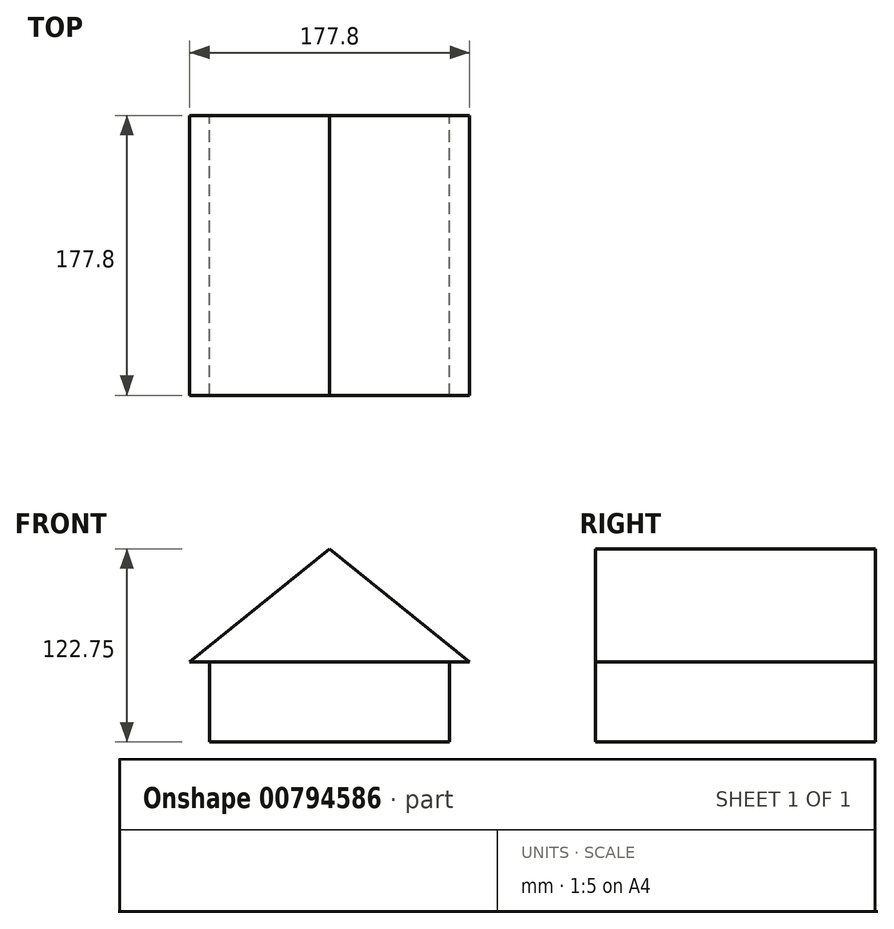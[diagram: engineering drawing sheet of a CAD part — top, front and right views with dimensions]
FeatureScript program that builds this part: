
annotation { "Feature Type Name" : "Feature", "Feature Type Description" : "" }
export const myFeature = defineFeature(function(context is Context, id is Id, definition is map)
    precondition{}
    {
        {
            var Q0;
            Q0=qCreatedBy(makeId("Front.planeOp"),FACE);
            var sketch = newSketch(context, id + "F0", { "sketchPlane" : qUnion([Q0])});
            skLineSegment(sketch, "E0.bottom", {"start": v(-76.34, 0) * mm, "end": v(76.06, 0) * mm});
            skLineSegment(sketch, "E0.top", {"start": v(-76.34, 50.8) * mm, "end": v(76.06, 50.8) * mm});
            skLineSegment(sketch, "E0.left", {"start": v(-76.34, 0) * mm, "end": v(-76.34, 50.8) * mm});
            skLineSegment(sketch, "E0.right", {"start": v(76.06, 0) * mm, "end": v(76.06, 50.8) * mm});
            skLineSegment(sketch, "E1.0", {"start": v(88.9, 50.9) * mm, "end": v(-88.9, 50.9) * mm});
            skLineSegment(sketch, "E1.1", {"start": v(-88.9, 50.9) * mm, "end": v(0, 122.75) * mm});
            skLineSegment(sketch, "E1.2", {"start": v(0, 122.75) * mm, "end": v(88.9, 50.9) * mm});
            skSolve(sketch);
        }
        {
            var Q0;
            Q0=makeQuery(id+"F0.imprint","IMPRINT",FACE,{"disambiguationData":[TD([[makeQuery(id+"F0.imprint","IMPRINT",EDGE,{"derivedFrom":sQuery(id+"F0.wireOp",EDGE,"E0.bottom")}),1.0]])]});
            extrude(context, id + "F1", {"entities" : qUnion([Q0]), "endBound" : BoundingType.SYMMETRIC, "depth" : 152.4 * mm, "offsetDistance" : 25.4 * mm});
        }
        {
            var Q0;
            Q0 = qSketchRegion(id + "F0", true);
            extrude(context, id + "F2", {"entities" : qUnion([Q0]), "operationType" : NewBodyOperationType.ADD, "endBound" : BoundingType.SYMMETRIC, "depth" : 177.8 * mm, "offsetDistance" : 25.4 * mm});
        }
    });
